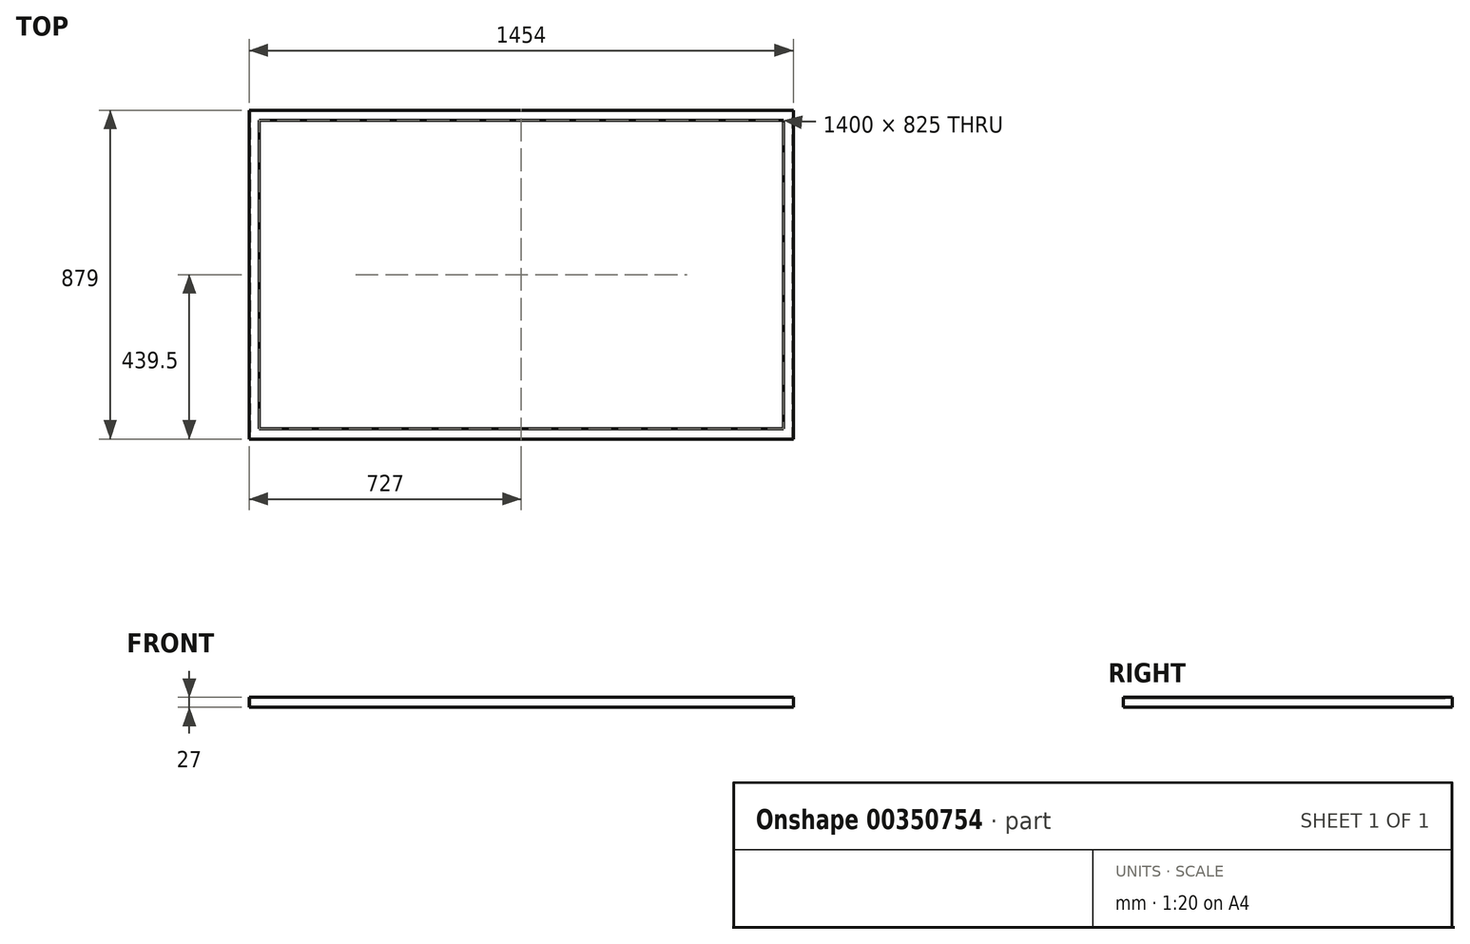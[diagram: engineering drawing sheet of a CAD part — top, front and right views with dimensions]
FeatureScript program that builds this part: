
annotation { "Feature Type Name" : "Feature", "Feature Type Description" : "" }
export const myFeature = defineFeature(function(context is Context, id is Id, definition is map)
    precondition{}
    {
        {
            var Q0;
            Q0=qCreatedBy(makeId("Top.planeOp"),FACE);
            var sketch = newSketch(context, id + "F0", { "sketchPlane" : qUnion([Q0])});
            skLineSegment(sketch, "E0.bottom", {"start": v(725, 437.5) * mm, "end": v(-725, 437.5) * mm});
            skLineSegment(sketch, "E0.top", {"start": v(725, -437.5) * mm, "end": v(-725, -437.5) * mm});
            skLineSegment(sketch, "E0.left", {"start": v(725, 437.5) * mm, "end": v(725, -437.5) * mm});
            skLineSegment(sketch, "E0.right", {"start": v(-725, 437.5) * mm, "end": v(-725, -437.5) * mm});
            skPoint(sketch, "E0.middle", {"position": v(0, 0) * mm});
            skSolve(sketch);
        }
        {
            var Q0;
            Q0=makeQuery(id+"F0.imprint","IMPRINT",FACE,{"disambiguationData":[TD([[makeQuery(id+"F0.imprint","IMPRINT",EDGE,{"derivedFrom":sQuery(id+"F0.wireOp",EDGE,"E0.bottom")}),1.0]])]});
            extrude(context, id + "F1", {"entities" : qUnion([Q0]), "depth" : 25 * mm});
        }
        {
            var Q0;
            Q0=makeQuery(id+"F1.opExtrude","SWEPT_FACE",FACE,{"disambiguationData":[OSD([sQuery(id+"F0.wireOp",EDGE,"E0.left")])]});
            var sketch = newSketch(context, id + "F2", { "sketchPlane" : qUnion([Q0])});
            skLineSegment(sketch, "E1", {"start": v(412.5, 25) * mm, "end": v(437.5, 25) * mm});
            skLineSegment(sketch, "E2", {"start": v(437.5, 25) * mm, "end": v(437.5, 0) * mm});
            skLineSegment(sketch, "E3", {"start": v(437.5, 0) * mm, "end": v(439.5, 0) * mm});
            skLineSegment(sketch, "E4", {"start": v(439.5, 0) * mm, "end": v(439.5, 27) * mm});
            skLineSegment(sketch, "E5", {"start": v(439.5, 27) * mm, "end": v(412.5, 27) * mm});
            skLineSegment(sketch, "E6", {"start": v(412.5, 27) * mm, "end": v(412.5, 25) * mm});
            skSolve(sketch);
        }
        {
            var Q0;
            Q0 = qSketchRegion(id + "F2", true);
            var Q1;
            Q1=makeQuery(id+"F1.opExtrude","CAP_EDGE",EDGE,{"disambiguationData":[OSD([sQuery(id+"F0.wireOp",EDGE,"E0.bottom")])],"isStart":false});
            var Q2;
            Q2=makeQuery(id+"F1.opExtrude","CAP_EDGE",EDGE,{"disambiguationData":[OSD([sQuery(id+"F0.wireOp",EDGE,"E0.right")])],"isStart":false});
            var Q3;
            Q3=makeQuery(id+"F1.opExtrude","CAP_EDGE",EDGE,{"disambiguationData":[OSD([sQuery(id+"F0.wireOp",EDGE,"E0.top")])],"isStart":false});
            var Q4;
            Q4=makeQuery(id+"F1.opExtrude","CAP_EDGE",EDGE,{"disambiguationData":[OSD([sQuery(id+"F0.wireOp",EDGE,"E0.left")])],"isStart":false});
            sweep(context, id + "F3", {"profiles" : qUnion([Q0]), "path" : qUnion([Q1, Q2, Q3, Q4])});
        }
    });
